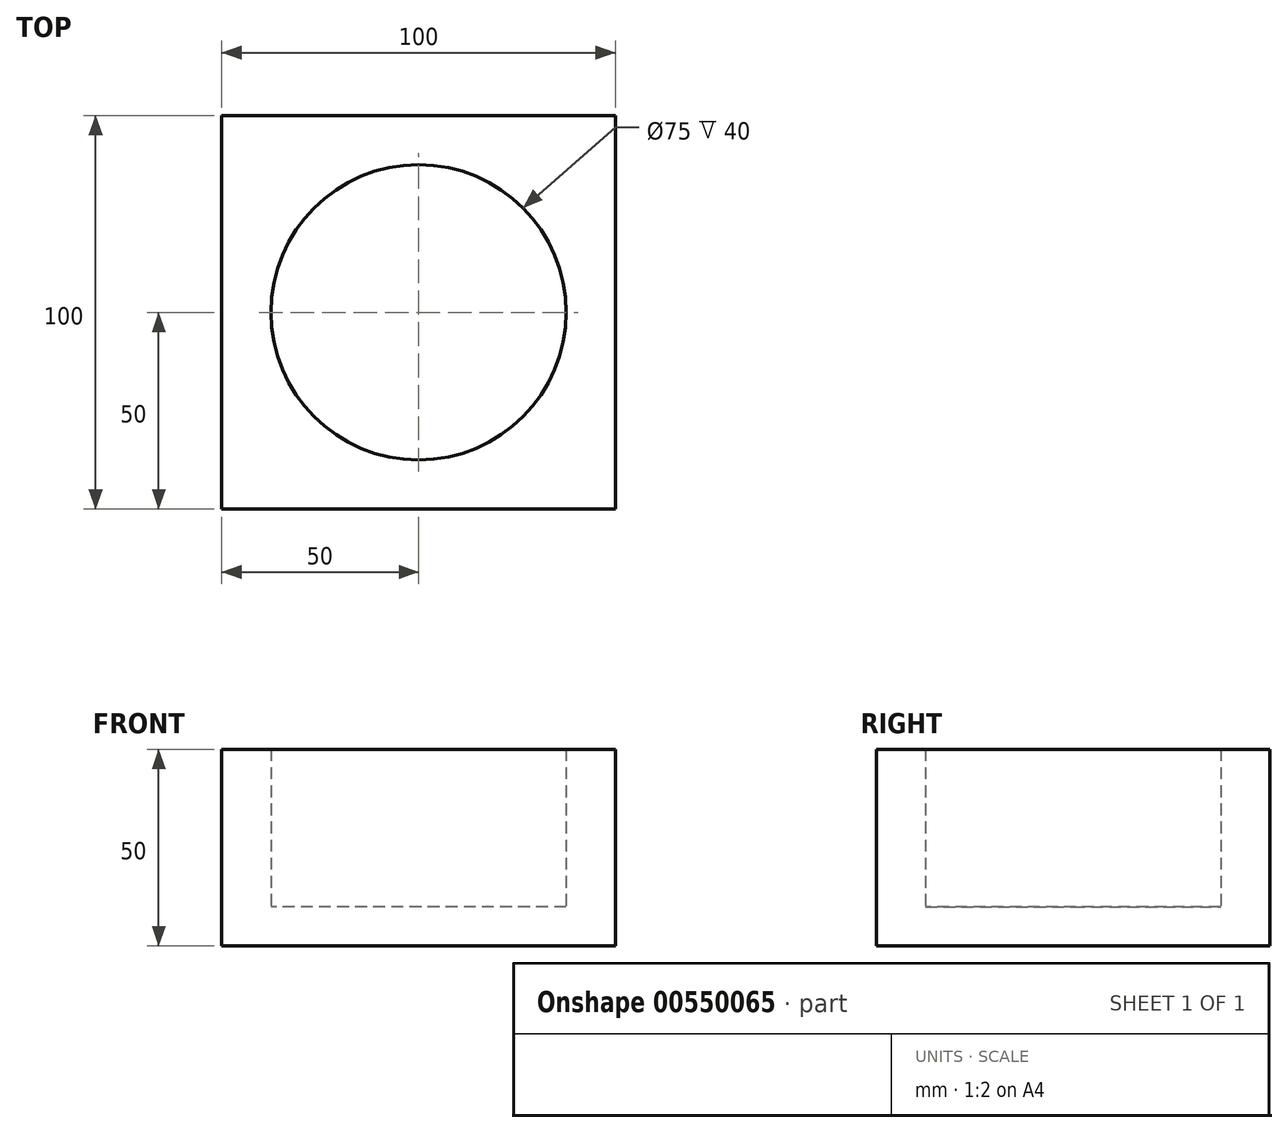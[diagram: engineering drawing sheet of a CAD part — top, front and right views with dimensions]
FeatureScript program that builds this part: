
annotation { "Feature Type Name" : "Feature", "Feature Type Description" : "" }
export const myFeature = defineFeature(function(context is Context, id is Id, definition is map)
    precondition{}
    {
        {
            var Q0;
            Q0=qCreatedBy(makeId("Top.planeOp"),FACE);
            var sketch = newSketch(context, id + "F0", { "sketchPlane" : qUnion([Q0])});
            skLineSegment(sketch, "E0.bottom", {"start": v(50, -50) * mm, "end": v(-50, -50) * mm});
            skLineSegment(sketch, "E0.top", {"start": v(50, 50) * mm, "end": v(-50, 50) * mm});
            skLineSegment(sketch, "E0.left", {"start": v(50, -50) * mm, "end": v(50, 50) * mm});
            skLineSegment(sketch, "E0.right", {"start": v(-50, -50) * mm, "end": v(-50, 50) * mm});
            skPoint(sketch, "E0.middle", {"position": v(0, 0) * mm});
            skCircle(sketch, "E1", {"center": v(0, 0) * mm, "radius": 37.5 * mm});
            skSolve(sketch);
        }
        {
            var Q0;
            Q0=makeQuery(id+"F0.imprint","IMPRINT",FACE,{"disambiguationData":[TD([[makeQuery(id+"F0.imprint","IMPRINT",EDGE,{"derivedFrom":sQuery(id+"F0.wireOp",EDGE,"E0.bottom")}),-1.0]])]});
            extrude(context, id + "F1", {"entities" : qUnion([Q0]), "depth" : 50 * mm, "offsetDistance" : 25 * mm});
        }
        {
            var Q0;
            Q0=makeQuery(id+"F0.imprint","IMPRINT",FACE,{"disambiguationData":[TD([[makeQuery(id+"F0.imprint","IMPRINT",EDGE,{"derivedFrom":sQuery(id+"F0.wireOp",EDGE,"E1")}),1.0]])]});
            extrude(context, id + "F2", {"entities" : qUnion([Q0]), "operationType" : NewBodyOperationType.ADD, "depth" : 10 * mm, "offsetDistance" : 25 * mm});
        }
    });
